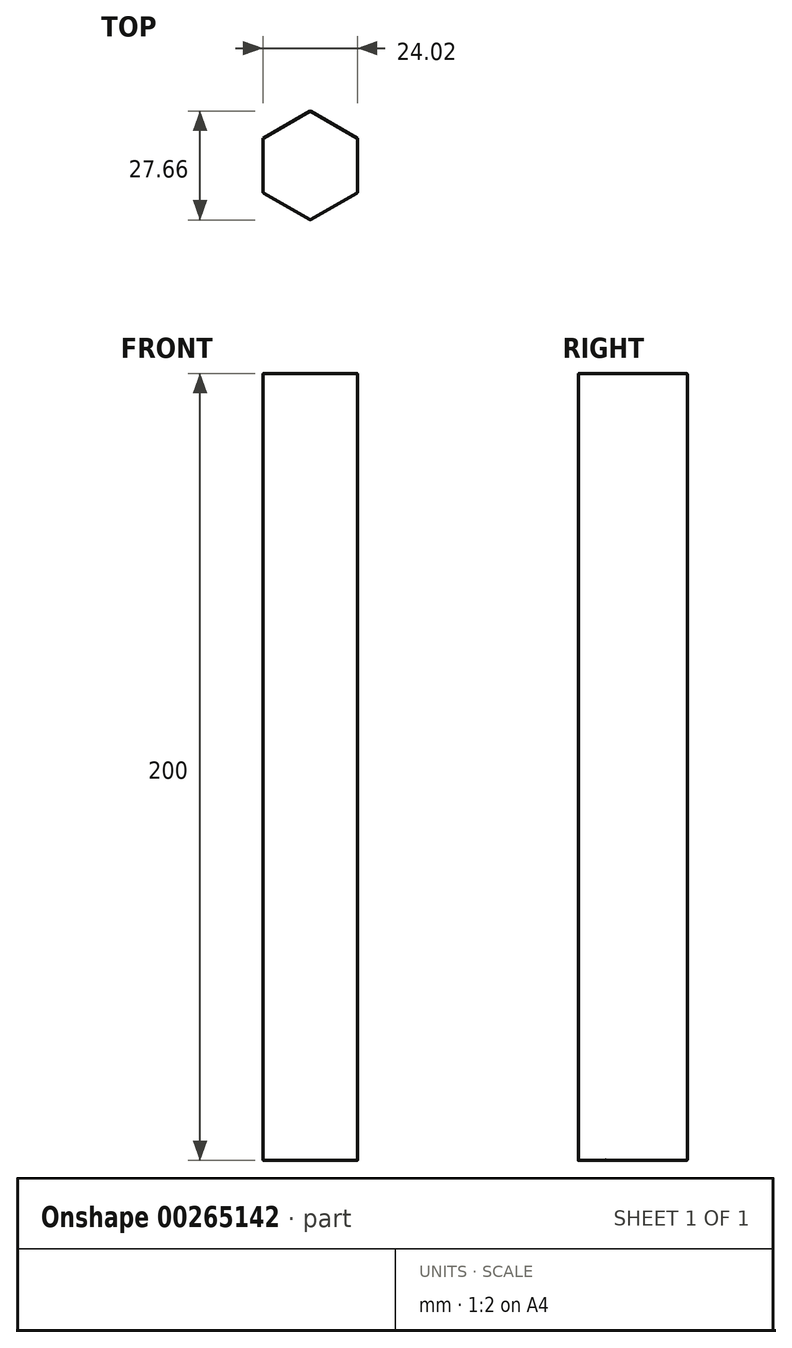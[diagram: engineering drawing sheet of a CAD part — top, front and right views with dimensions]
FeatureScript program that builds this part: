
annotation { "Feature Type Name" : "Feature", "Feature Type Description" : "" }
export const myFeature = defineFeature(function(context is Context, id is Id, definition is map)
    precondition{}
    {
        {
            var Q0;
            Q0=qCreatedBy(makeId("Top.planeOp"),FACE);
            var sketch = newSketch(context, id + "F0", { "sketchPlane" : qUnion([Q0])});
            skCircle(sketch, "E0.cCircle", {"center": v(0, 0) * mm, "radius": 12 * mm, "construction": true});
            skLineSegment(sketch, "E0.0", {"start": v(12, -6.94) * mm, "end": v(-0.02, -13.86) * mm});
            skLineSegment(sketch, "E0.1", {"start": v(-0.02, -13.86) * mm, "end": v(-12, -6.91) * mm});
            skLineSegment(sketch, "E0.2", {"start": v(-12, -6.91) * mm, "end": v(-12, 6.94) * mm});
            skLineSegment(sketch, "E0.3", {"start": v(-12, 6.94) * mm, "end": v(0.02, 13.86) * mm});
            skLineSegment(sketch, "E0.4", {"start": v(0.02, 13.86) * mm, "end": v(12, 6.91) * mm});
            skLineSegment(sketch, "E0.5", {"start": v(12, 6.91) * mm, "end": v(12, -6.94) * mm});
            skPoint(sketch, "E0.0.midPoint", {"position": v(5.99, -10.4) * mm});
            skSolve(sketch);
        }
        {
            var Q0;
            Q0 = qSketchRegion(id + "F0", true);
            extrude(context, id + "F1", {"entities" : qUnion([Q0]), "depth" : 200 * mm});
        }
        {
            var Q0;
            Q0=makeQuery(id+"F1.opExtrude","CAP_FACE",FACE,{"disambiguationData":[OSD([sQuery(id+"F0.wireOp",EDGE,"E0.0"),sQuery(id+"F0.wireOp",EDGE,"E0.1"),sQuery(id+"F0.wireOp",EDGE,"E0.2"),sQuery(id+"F0.wireOp",EDGE,"E0.3"),sQuery(id+"F0.wireOp",EDGE,"E0.4"),sQuery(id+"F0.wireOp",EDGE,"E0.5")])],"isStart":false});
            var Q1;
            Q1=makeQuery(id+"F1.opExtrude","SWEPT_FACE",FACE,{"disambiguationData":[OSD([sQuery(id+"F0.wireOp",EDGE,"E0.5")])]});
            var Q2;
            Q2=makeQuery(id+"F1.opExtrude","SWEPT_FACE",FACE,{"disambiguationData":[OSD([sQuery(id+"F0.wireOp",EDGE,"E0.4")])]});
            var Q3;
            Q3=makeQuery(id+"F1.opExtrude","SWEPT_FACE",FACE,{"disambiguationData":[OSD([sQuery(id+"F0.wireOp",EDGE,"E0.3")])]});
            var Q4;
            Q4=makeQuery(id+"F1.opExtrude","SWEPT_FACE",FACE,{"disambiguationData":[OSD([sQuery(id+"F0.wireOp",EDGE,"E0.2")])]});
            var Q5;
            Q5=makeQuery(id+"F1.opExtrude","SWEPT_FACE",FACE,{"disambiguationData":[OSD([sQuery(id+"F0.wireOp",EDGE,"E0.1")])]});
            fillet(context, id + "F2", {"entities" : qUnion([Q0, Q1, Q2, Q3, Q4, Q5]), "radius" : .2 * mm, "tangentPropagation" : true, "allowEdgeOverflow" : false});
        }
    });
